# Revit family: Door_Coiling_UltiGroup_UltiRoll_HighSpeedDoor_Entry M09
name_source: partatom
category: Doors
revit_build: Autodesk Revit 2018 (Build: 20170223_1515(x64)
units: mm (PartAtom-declared; Revit-internal decimal feet)

## family parameters
Always vertical = Yes
Cut with Voids When Loaded = No
Host = Wall
OmniClass Number = 23.30.10.17.27.11
OmniClass Title = Overhead Coiling
Room Calculation Point = No
Shared = No

## types (1)
- Type 1
    Analytic Construction = <None>
    Bottom edge material = Bottom edge material
    Control Box height = 1150 mm
    Curtain guide material = Curtain guide material
    Description = Roll Entry M09
    Door open = 129 mm
    DoorFrameMaterial_ANZRS = Door Frame finish
    DoorFrameType_ANZRS = Stainless Steel or Galvanized Steel Frame
    DoorGlazingHeight_ANZRS = 0 mm  [stored 0 ft]
    DoorGlazingType_ANZRS = Stainless Steel or Painted
    DoorGlazingWidth_ANZRS = 0 mm  [stored 0 ft]
    DoorGrilleHeight_ANZRS = 0 mm  [stored 0 ft]
    DoorGrilleWidth_ANZRS = 0 mm  [stored 0 ft]
    DoorGrille_ANZRS = No
    DoorNumberOfPanels_ANZRS = 0
    DoorOperation_ANZRS = [OPEN-CLOSE push button][Pneumatically activated with Safety Edge][Manual opening by means of counter weight]
    DoorPanelBWidth_ANZRS = 0 mm  [stored 0 ft]
    DoorPanelDepth_ANZRS = 0 mm  [stored 0 ft]
    DoorPanelFinish_ANZRS = PVC Fabric curtain with colour option
    DoorPanelHeight_ANZRS = 0 mm  [stored 0 ft]
    DoorPanelMaterial_ANZRS = Door Curtain colour
    DoorPanelWidth_ANZRS = 0 mm  [stored 0 ft]
    Fax = 07 846 2467
    Function = Interior
    Height = 2051 mm  [stored 6.729 ft]
    InstallationGroup_ANZRS = 0
    Manufacturer = Ulti Group Ltd. / Monban
    Model = Ulti Roll Entry
    ModifiedIssue_ANZRS = 0 $
    Overall door width = 1300 mm  [stored 4.26509 ft]
    Send Message = http://ultigroup.co.nz
    URL = www.ultigroup.co.nz
    Vision Panel height = 1130 mm  [stored 3.70735 ft]
    Wall Closure = By host
    Width = 1200 mm  [stored 3.93701 ft]

note: [stored X ft] marks values corroborated as IEEE doubles in the binary element streams (Revit-internal decimal feet)

## geometry (parser evidence)
native form markers: Blend x4, Sweep x54
no freeform markers — native parametric forms only
